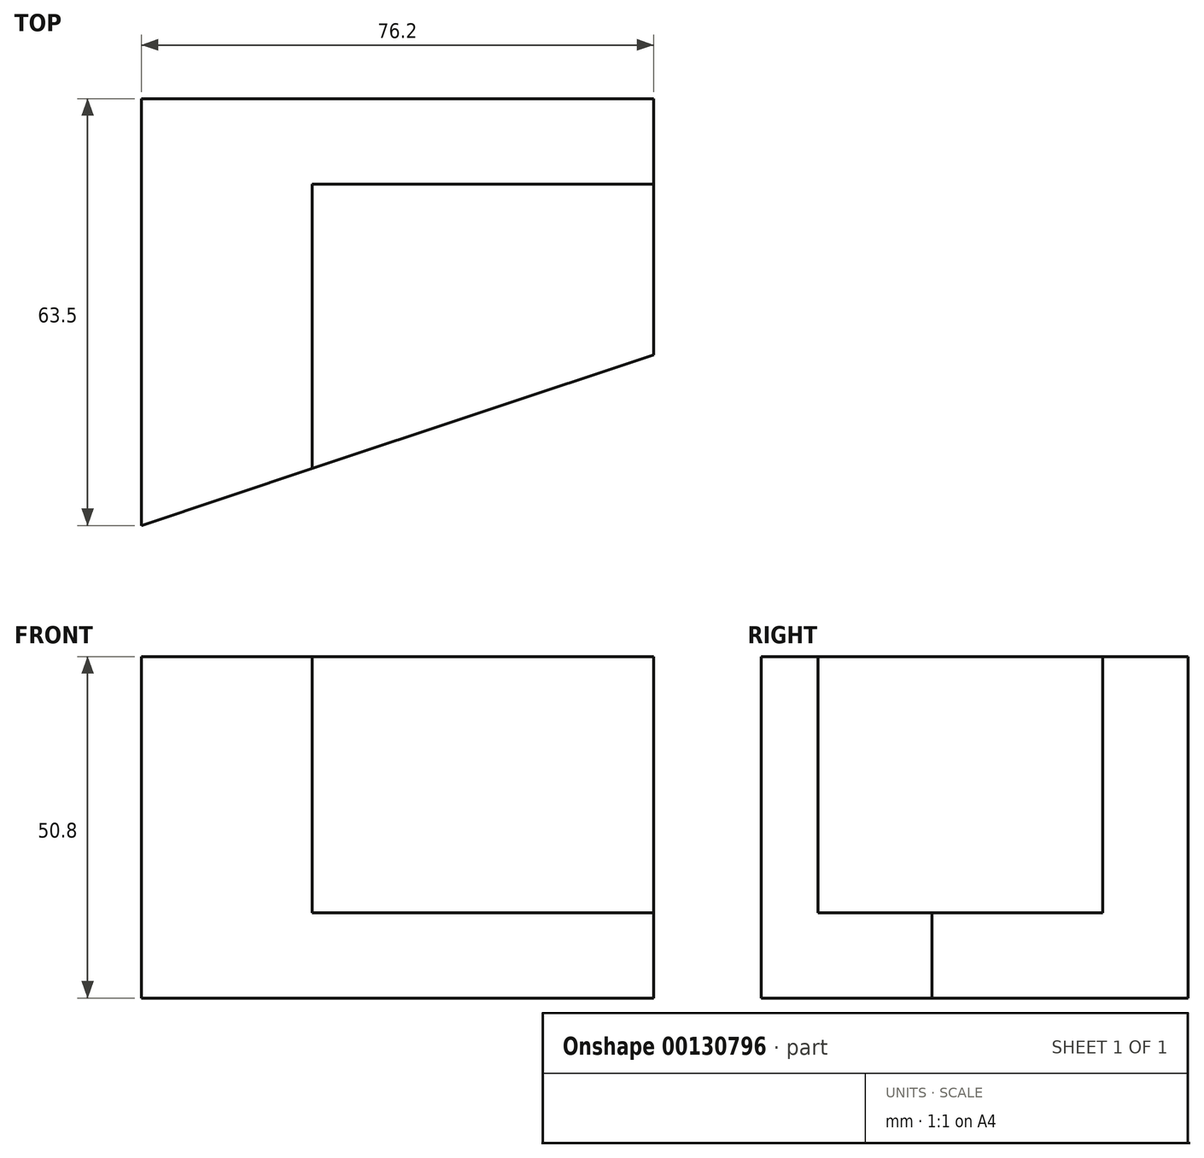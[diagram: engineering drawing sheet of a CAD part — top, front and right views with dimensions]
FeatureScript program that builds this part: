
annotation { "Feature Type Name" : "Feature", "Feature Type Description" : "" }
export const myFeature = defineFeature(function(context is Context, id is Id, definition is map)
    precondition{}
    {
        {
            var Q0;
            Q0=qCreatedBy(makeId("Top.planeOp"),FACE);
            var sketch = newSketch(context, id + "F0", { "sketchPlane" : qUnion([Q0])});
            skLineSegment(sketch, "E0", {"start": v(0, 0) * mm, "end": v(0, 63.5) * mm});
            skLineSegment(sketch, "E1", {"start": v(0, 63.5) * mm, "end": v(76.2, 63.5) * mm});
            skLineSegment(sketch, "E2", {"start": v(76.2, 63.5) * mm, "end": v(76.2, 50.8) * mm});
            skLineSegment(sketch, "E3", {"start": v(76.2, 50.8) * mm, "end": v(25.4, 50.8) * mm});
            skLineSegment(sketch, "E4", {"start": v(76.2, 50.8) * mm, "end": v(76.2, 25.4) * mm});
            skLineSegment(sketch, "E5", {"start": v(25.4, 50.8) * mm, "end": v(25.4, 8.47) * mm});
            skLineSegment(sketch, "E6", {"start": v(76.2, 25.4) * mm, "end": v(0, 0) * mm});
            skSolve(sketch);
        }
        {
            var Q0;
            {var subQ0=sQuery(id+"F0.wireOp",EDGE,"E0");Q0=makeQuery(id+"F0.imprint","IMPRINT",FACE,{"disambiguationData":[TD([[makeQuery(id+"F0.imprint","IMPRINT",EDGE,{"derivedFrom":subQ0}),-1.0]])]});}
            extrude(context, id + "F1", {"entities" : qUnion([Q0]), "depth" : 50.8 * mm});
        }
        {
            var Q0;
            Q0=makeQuery(id+"F0.imprint","IMPRINT",FACE,{"disambiguationData":[TD([[makeQuery(id+"F0.imprint","IMPRINT",EDGE,{"derivedFrom":sQuery(id+"F0.wireOp",EDGE,"E3")}),1.0]])]});
            extrude(context, id + "F2", {"entities" : qUnion([Q0]), "operationType" : NewBodyOperationType.ADD, "depth" : 12.7 * mm});
        }
    });
